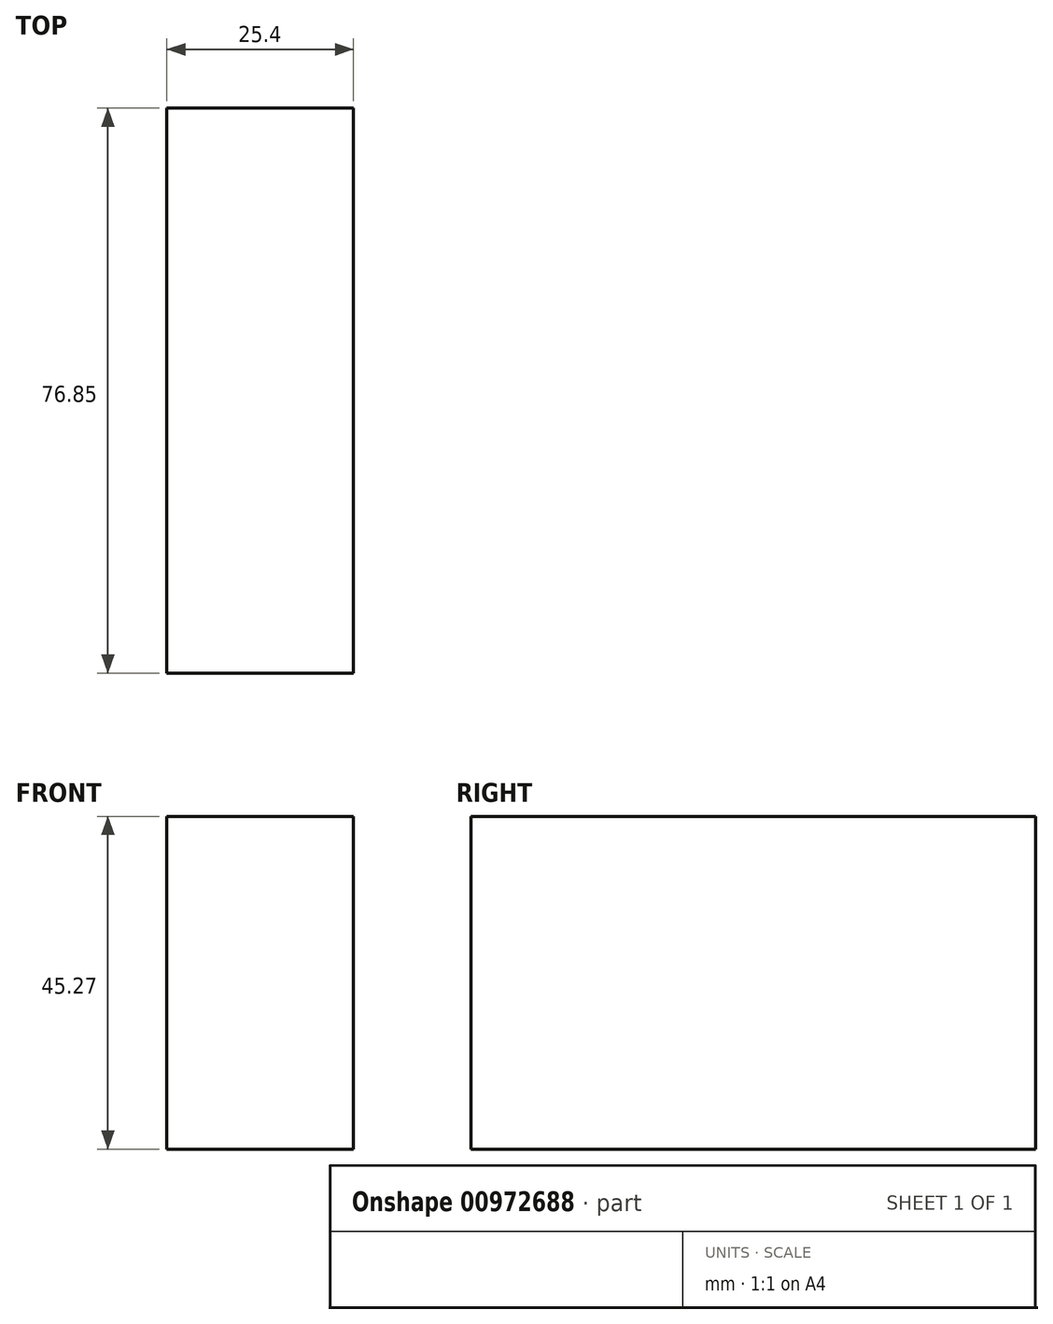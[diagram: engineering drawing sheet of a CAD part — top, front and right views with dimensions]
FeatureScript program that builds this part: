
annotation { "Feature Type Name" : "Feature", "Feature Type Description" : "" }
export const myFeature = defineFeature(function(context is Context, id is Id, definition is map)
    precondition{}
    {
        {
            var Q0;
            Q0=qCreatedBy(makeId("Right.planeOp"),FACE);
            var sketch = newSketch(context, id + "F0", { "sketchPlane" : qUnion([Q0])});
            skLineSegment(sketch, "E0.bottom", {"start": v(0, 0) * mm, "end": v(-76.85, 0) * mm});
            skLineSegment(sketch, "E0.top", {"start": v(0, 45.27) * mm, "end": v(-76.85, 45.27) * mm});
            skLineSegment(sketch, "E0.left", {"start": v(0, 0) * mm, "end": v(0, 45.27) * mm});
            skLineSegment(sketch, "E0.right", {"start": v(-76.85, 0) * mm, "end": v(-76.85, 45.27) * mm});
            skSolve(sketch);
        }
        {
            var Q0;
            Q0 = qSketchRegion(id + "F0", true);
            extrude(context, id + "F1", {"entities" : qUnion([Q0]), "depth" : 25.4 * mm, "offsetDistance" : 25.4 * mm});
        }
    });
